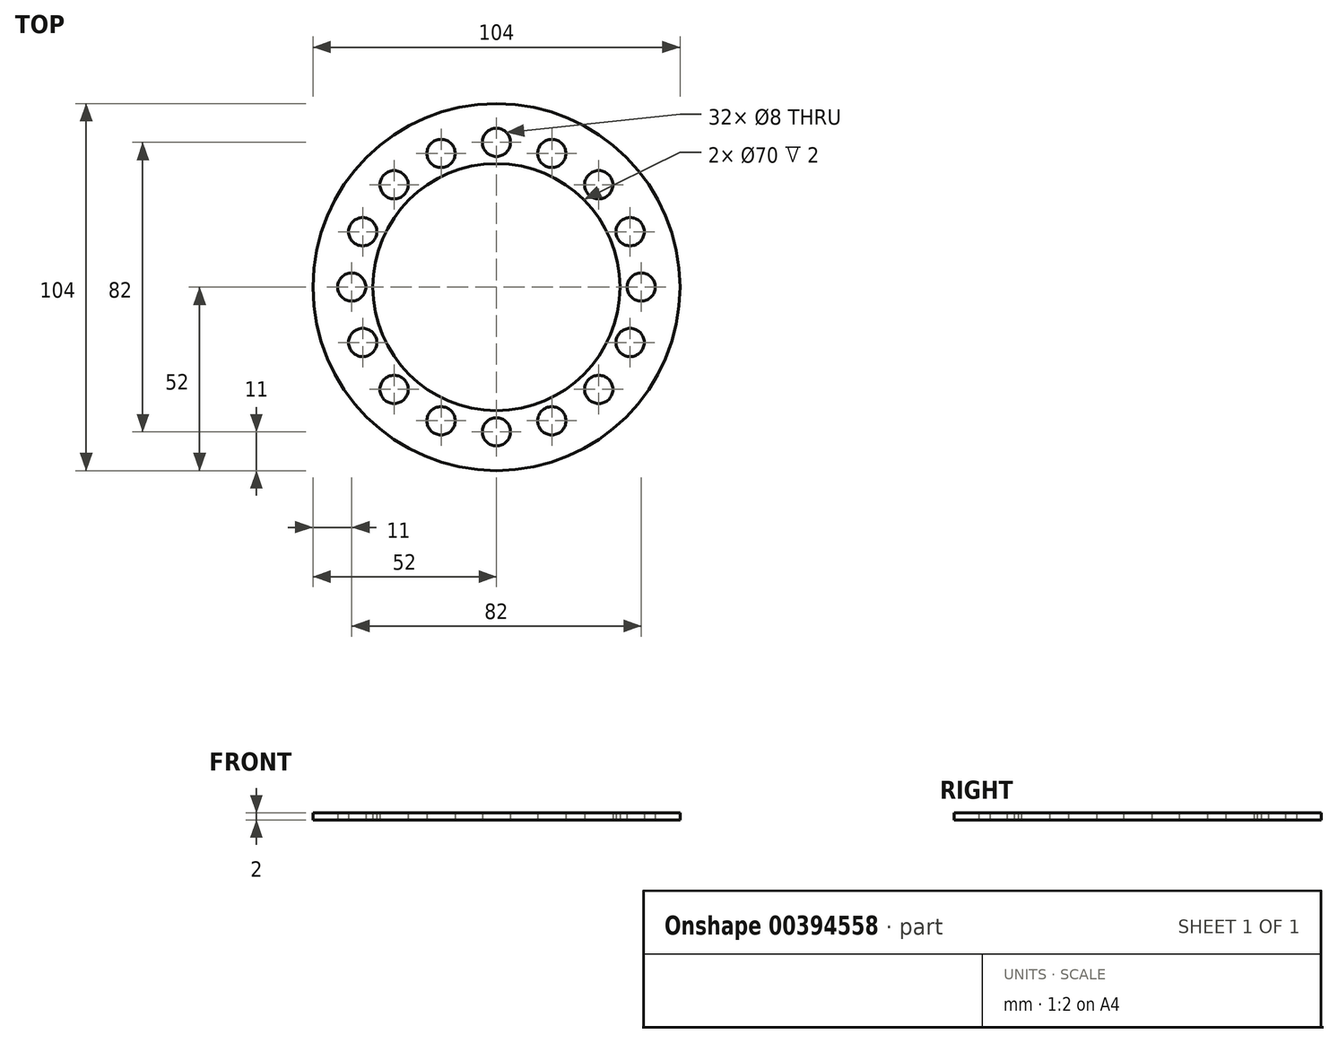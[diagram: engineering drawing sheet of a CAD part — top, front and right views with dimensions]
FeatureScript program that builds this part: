
annotation { "Feature Type Name" : "Feature", "Feature Type Description" : "" }
export const myFeature = defineFeature(function(context is Context, id is Id, definition is map)
    precondition{}
    {
        {
            var Q0;
            Q0=qCreatedBy(makeId("Top.planeOp"),FACE);
            var sketch = newSketch(context, id + "F0", { "sketchPlane" : qUnion([Q0])});
            skCircle(sketch, "E0", {"center": v(0, 0) * mm, "radius": 52 * mm});
            skCircle(sketch, "E1", {"center": v(0, 0) * mm, "radius": 35 * mm});
            skCircle(sketch, "E2", {"center": v(0, 41) * mm, "radius": 4 * mm});
            skCircle(sketch, "E3.1.0", {"center": v(-15.7, 37.88) * mm, "radius": 4 * mm});
            skCircle(sketch, "E3.2.0", {"center": v(-29, 29) * mm, "radius": 4 * mm});
            skCircle(sketch, "E3.3.0", {"center": v(-37.88, 15.7) * mm, "radius": 4 * mm});
            skCircle(sketch, "E3.4.0", {"center": v(-41, 0) * mm, "radius": 4 * mm});
            skCircle(sketch, "E3.5.0", {"center": v(-37.88, -15.7) * mm, "radius": 4 * mm});
            skCircle(sketch, "E3.6.0", {"center": v(-29, -29) * mm, "radius": 4 * mm});
            skCircle(sketch, "E3.7.0", {"center": v(-15.7, -37.88) * mm, "radius": 4 * mm});
            skCircle(sketch, "E3.8.0", {"center": v(0, -41) * mm, "radius": 4 * mm});
            skCircle(sketch, "E3.9.0", {"center": v(15.7, -37.88) * mm, "radius": 4 * mm});
            skCircle(sketch, "E3.10.0", {"center": v(29, -29) * mm, "radius": 4 * mm});
            skCircle(sketch, "E3.11.0", {"center": v(37.88, -15.7) * mm, "radius": 4 * mm});
            skCircle(sketch, "E3.12.0", {"center": v(41, 0) * mm, "radius": 4 * mm});
            skCircle(sketch, "E3.13.0", {"center": v(37.88, 15.7) * mm, "radius": 4 * mm});
            skCircle(sketch, "E3.14.0", {"center": v(29, 29) * mm, "radius": 4 * mm});
            skCircle(sketch, "E3.15.0", {"center": v(15.7, 37.88) * mm, "radius": 4 * mm});
            skSolve(sketch);
        }
        {
            var Q0;
            Q0=makeQuery(id+"F0.imprint","IMPRINT",FACE,{"disambiguationData":[TD([[makeQuery(id+"F0.imprint","IMPRINT",EDGE,{"derivedFrom":sQuery(id+"F0.wireOp",EDGE,"E0")}),1.0]])]});
            extrude(context, id + "F1", {"entities" : qUnion([Q0]), "depth" : 2 * mm});
        }
        {
            var Q0;
            Q0=makeQuery(id+"F0.imprint","IMPRINT",FACE,{"disambiguationData":[TD([[makeQuery(id+"F0.imprint","IMPRINT",EDGE,{"derivedFrom":sQuery(id+"F0.wireOp",EDGE,"E0")}),1.0]])]});
            extrude(context, id + "F2", {"entities" : qUnion([Q0]), "depth" : 2 * mm});
        }
    });
